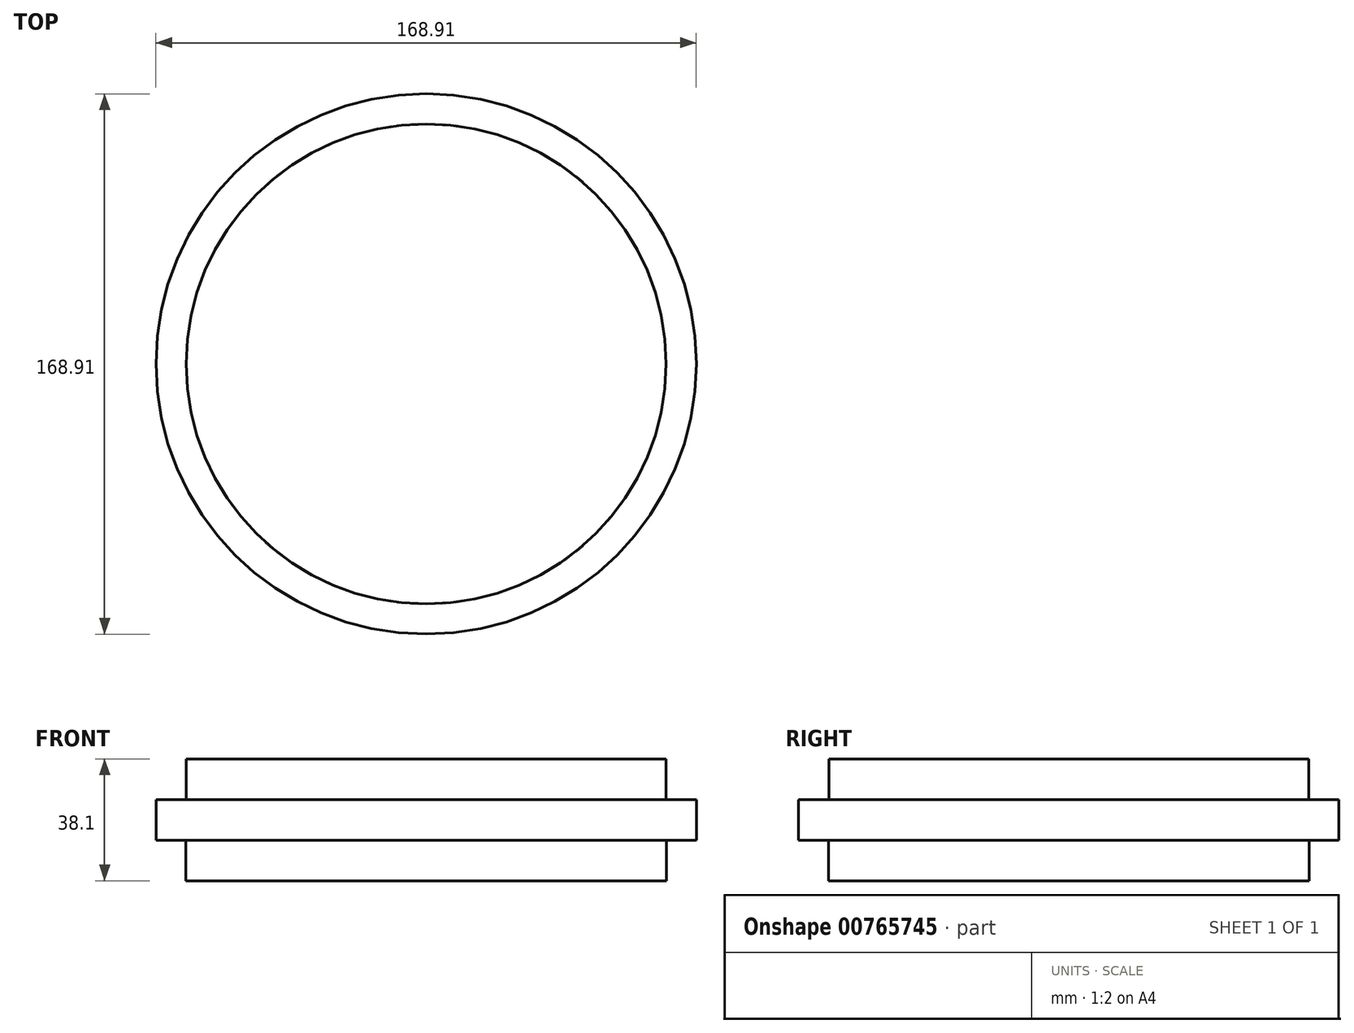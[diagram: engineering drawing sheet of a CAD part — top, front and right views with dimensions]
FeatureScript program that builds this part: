
annotation { "Feature Type Name" : "Feature", "Feature Type Description" : "" }
export const myFeature = defineFeature(function(context is Context, id is Id, definition is map)
    precondition{}
    {
        {
            var Q0;
            Q0=qCreatedBy(makeId("Top.planeOp"),FACE);
            var sketch = newSketch(context, id + "F0", { "sketchPlane" : qUnion([Q0])});
            skCircle(sketch, "E0", {"center": v(-62.6, 40.88) * mm, "radius": 84.45 * mm});
            skSolve(sketch);
        }
        {
            var Q0;
            Q0=makeQuery(id+"F0.imprint","IMPRINT",FACE,{"disambiguationData":[TD([[makeQuery(id+"F0.imprint","IMPRINT",EDGE,{"derivedFrom":sQuery(id+"F0.wireOp",EDGE,"E0")}),1.0]])]});
            var sketch = newSketch(context, id + "F1", { "sketchPlane" : qUnion([Q0])});
            skSolve(sketch);
        }
        {
            var Q0;
            Q0=makeQuery(id+"F0.imprint","IMPRINT",FACE,{"disambiguationData":[TD([[makeQuery(id+"F0.imprint","IMPRINT",EDGE,{"derivedFrom":sQuery(id+"F0.wireOp",EDGE,"E0")}),1.0]])]});
            var sketch = newSketch(context, id + "F2", { "sketchPlane" : qUnion([Q0])});
            skSolve(sketch);
        }
        {
            var Q0;
            Q0 = qSketchRegion(id + "F2", true);
            var Q1;
            Q1=makeQuery(id+"F0.imprint","IMPRINT",FACE,{"disambiguationData":[TD([[makeQuery(id+"F0.imprint","IMPRINT",EDGE,{"derivedFrom":sQuery(id+"F0.wireOp",EDGE,"E0")}),1.0]])]});
            var Q2;
            Q2=makeQuery(id+"F1.imprint","IMPRINT",FACE,{"disambiguationData":[TD([[makeQuery(id+"F1.imprint","IMPRINT",EDGE,{"derivedFrom":makeQuery(id+"F0.imprint","IMPRINT",EDGE,{"derivedFrom":sQuery(id+"F0.wireOp",EDGE,"E0")})}),1.0]])]});
            var Q3;
            Q3=makeQuery(id+"F2.imprint","IMPRINT",FACE,{"disambiguationData":[TD([[makeQuery(id+"F2.imprint","IMPRINT",EDGE,{"derivedFrom":makeQuery(id+"F0.imprint","IMPRINT",EDGE,{"derivedFrom":sQuery(id+"F0.wireOp",EDGE,"E0")})}),1.0]])]});
            extrude(context, id + "F3", {"entities" : qUnion([Q0, Q1, Q2, Q3]), "depth" : 12.7 * mm, "offsetDistance" : 25.4 * mm});
        }
        {
            var Q0;
            {var subQ0=sQuery(id+"F0.wireOp",EDGE,"E0");Q0=makeQuery(id+"F3.opExtrude","CAP_FACE",FACE,{"disambiguationData":[OSD([subQ0]),TDD([makeQuery(id+"F0.imprint","IMPRINT",EDGE,{"derivedFrom":subQ0})])],"isStart":true});}
            var sketch = newSketch(context, id + "F4", { "sketchPlane" : qUnion([Q0])});
            skCircle(sketch, "E1", {"center": v(-62.6, -40.88) * mm, "radius": 75.18 * mm});
            skSolve(sketch);
        }
        {
            var Q0;
            Q0=makeQuery(id+"F4.imprint","IMPRINT",FACE,{"disambiguationData":[TD([[makeQuery(id+"F4.imprint","IMPRINT",EDGE,{"derivedFrom":sQuery(id+"F4.wireOp",EDGE,"E1")}),1.0]])]});
            var sketch = newSketch(context, id + "F5", { "sketchPlane" : qUnion([Q0])});
            skSolve(sketch);
        }
        {
            var Q0;
            Q0=makeQuery(id+"F5.imprint","IMPRINT",FACE,{"disambiguationData":[TD([[makeQuery(id+"F5.imprint","IMPRINT",EDGE,{"derivedFrom":makeQuery(id+"F4.imprint","IMPRINT",EDGE,{"derivedFrom":sQuery(id+"F4.wireOp",EDGE,"E1")})}),1.0]])]});
            var sketch = newSketch(context, id + "F6", { "sketchPlane" : qUnion([Q0])});
            skSolve(sketch);
        }
        {
            var Q0;
            Q0 = qSketchRegion(id + "F6", true);
            var Q1;
            Q1=makeQuery(id+"F5.imprint","IMPRINT",FACE,{"disambiguationData":[TD([[makeQuery(id+"F5.imprint","IMPRINT",EDGE,{"derivedFrom":makeQuery(id+"F4.imprint","IMPRINT",EDGE,{"derivedFrom":sQuery(id+"F4.wireOp",EDGE,"E1")})}),1.0]])]});
            extrude(context, id + "F7", {"entities" : qUnion([Q0, Q1]), "depth" : 12.7 * mm, "offsetDistance" : 25.4 * mm});
        }
        {
            var Q0;
            {var subQ0=sQuery(id+"F0.wireOp",EDGE,"E0");Q0=makeQuery(id+"F3.opExtrude","CAP_FACE",FACE,{"disambiguationData":[OSD([subQ0]),TDD([makeQuery(id+"F0.imprint","IMPRINT",EDGE,{"derivedFrom":subQ0})])],"isStart":false});}
            var sketch = newSketch(context, id + "F8", { "sketchPlane" : qUnion([Q0])});
            skCircle(sketch, "E2", {"center": v(-62.6, 40.88) * mm, "radius": 75.03 * mm});
            skSolve(sketch);
        }
        {
            var Q0;
            Q0=makeQuery(id+"F8.imprint","IMPRINT",FACE,{"disambiguationData":[TD([[makeQuery(id+"F8.imprint","IMPRINT",EDGE,{"derivedFrom":sQuery(id+"F8.wireOp",EDGE,"E2")}),1.0]])]});
            var sketch = newSketch(context, id + "F9", { "sketchPlane" : qUnion([Q0])});
            skSolve(sketch);
        }
        {
            var Q0;
            Q0 = qSketchRegion(id + "F9", true);
            var Q1;
            Q1=makeQuery(id+"F9.imprint","IMPRINT",FACE,{"disambiguationData":[TD([[makeQuery(id+"F9.imprint","IMPRINT",EDGE,{"derivedFrom":makeQuery(id+"F8.imprint","IMPRINT",EDGE,{"derivedFrom":sQuery(id+"F8.wireOp",EDGE,"E2")})}),1.0]])]});
            extrude(context, id + "F10", {"entities" : qUnion([Q0, Q1]), "depth" : 12.7 * mm, "offsetDistance" : 25.4 * mm});
        }
    });
